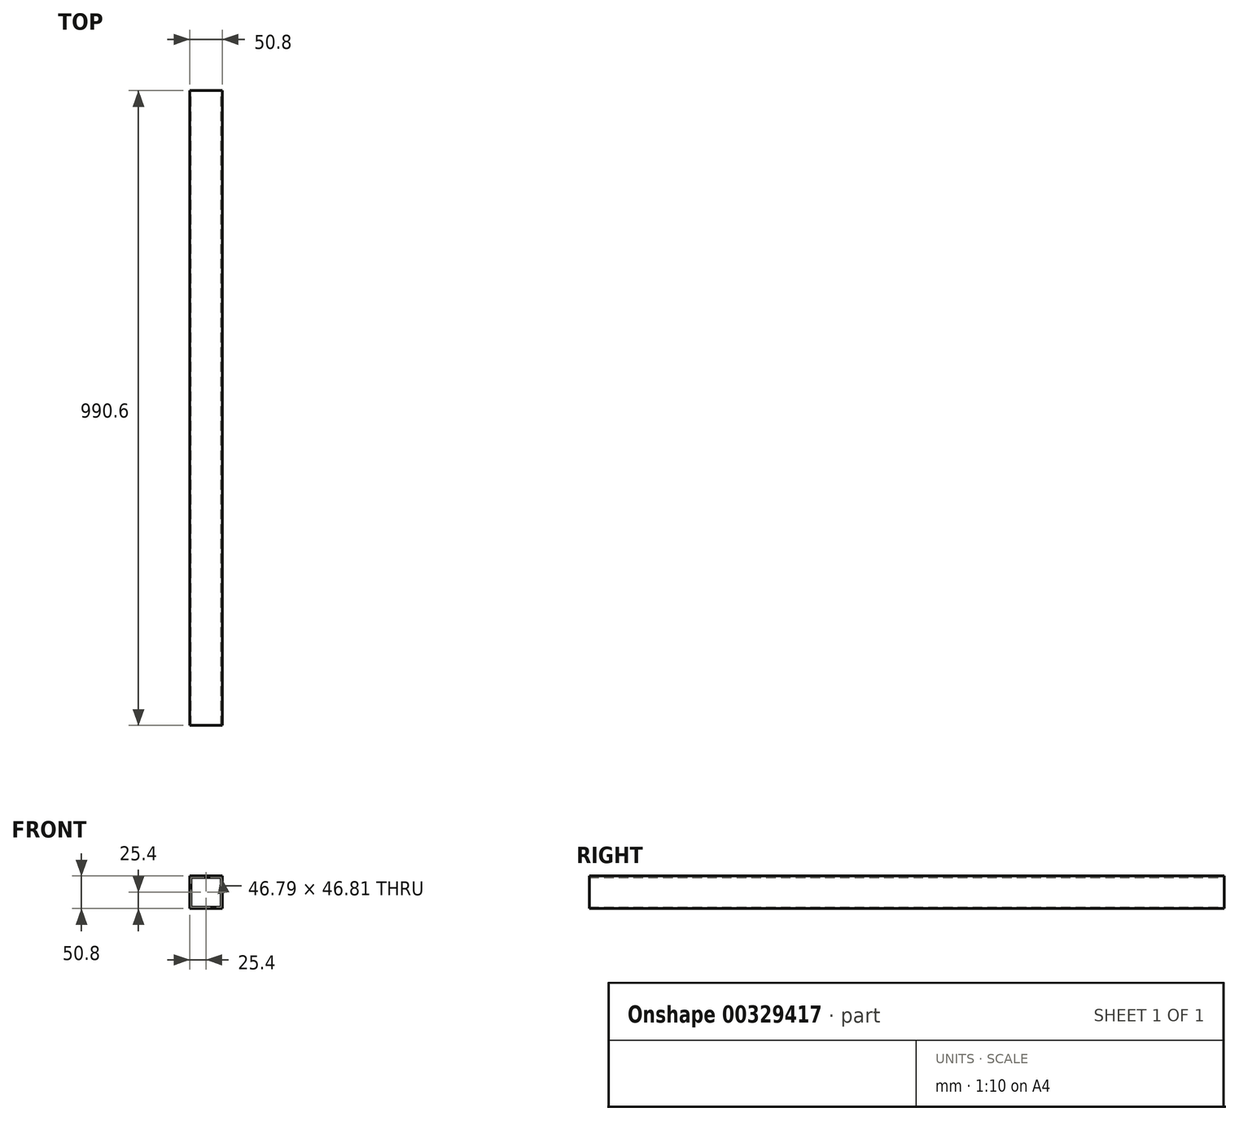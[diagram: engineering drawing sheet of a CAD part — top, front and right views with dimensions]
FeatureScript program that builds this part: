
annotation { "Feature Type Name" : "Feature", "Feature Type Description" : "" }
export const myFeature = defineFeature(function(context is Context, id is Id, definition is map)
    precondition{}
    {
        {
            var Q0;
            Q0=qCreatedBy(makeId("Front.planeOp"),FACE);
            var sketch = newSketch(context, id + "F0", { "sketchPlane" : qUnion([Q0])});
            skLineSegment(sketch, "E0.bottom", {"start": v(25.4, -25.4) * mm, "end": v(-25.4, -25.4) * mm});
            skLineSegment(sketch, "E0.top", {"start": v(25.4, 25.4) * mm, "end": v(-25.4, 25.4) * mm});
            skLineSegment(sketch, "E0.left", {"start": v(25.4, -25.4) * mm, "end": v(25.4, 25.4) * mm});
            skLineSegment(sketch, "E0.right", {"start": v(-25.4, -25.4) * mm, "end": v(-25.4, 25.4) * mm});
            skPoint(sketch, "E0.middle", {"position": v(0, 0) * mm});
            skLineSegment(sketch, "E1.bottom", {"start": v(23.4, -23.4) * mm, "end": v(-23.4, -23.4) * mm});
            skLineSegment(sketch, "E1.top", {"start": v(23.4, 23.4) * mm, "end": v(-23.4, 23.4) * mm});
            skLineSegment(sketch, "E1.left", {"start": v(23.4, -23.4) * mm, "end": v(23.4, 23.4) * mm});
            skLineSegment(sketch, "E1.right", {"start": v(-23.4, -23.4) * mm, "end": v(-23.4, 23.4) * mm});
            skSolve(sketch);
        }
        {
            var Q0;
            Q0=qSketchRegion(id+"F0",true);
            extrude(context, id + "F1", {"entities" : qUnion([Q0]), "depth" : 990.6 * mm});
        }
    });
